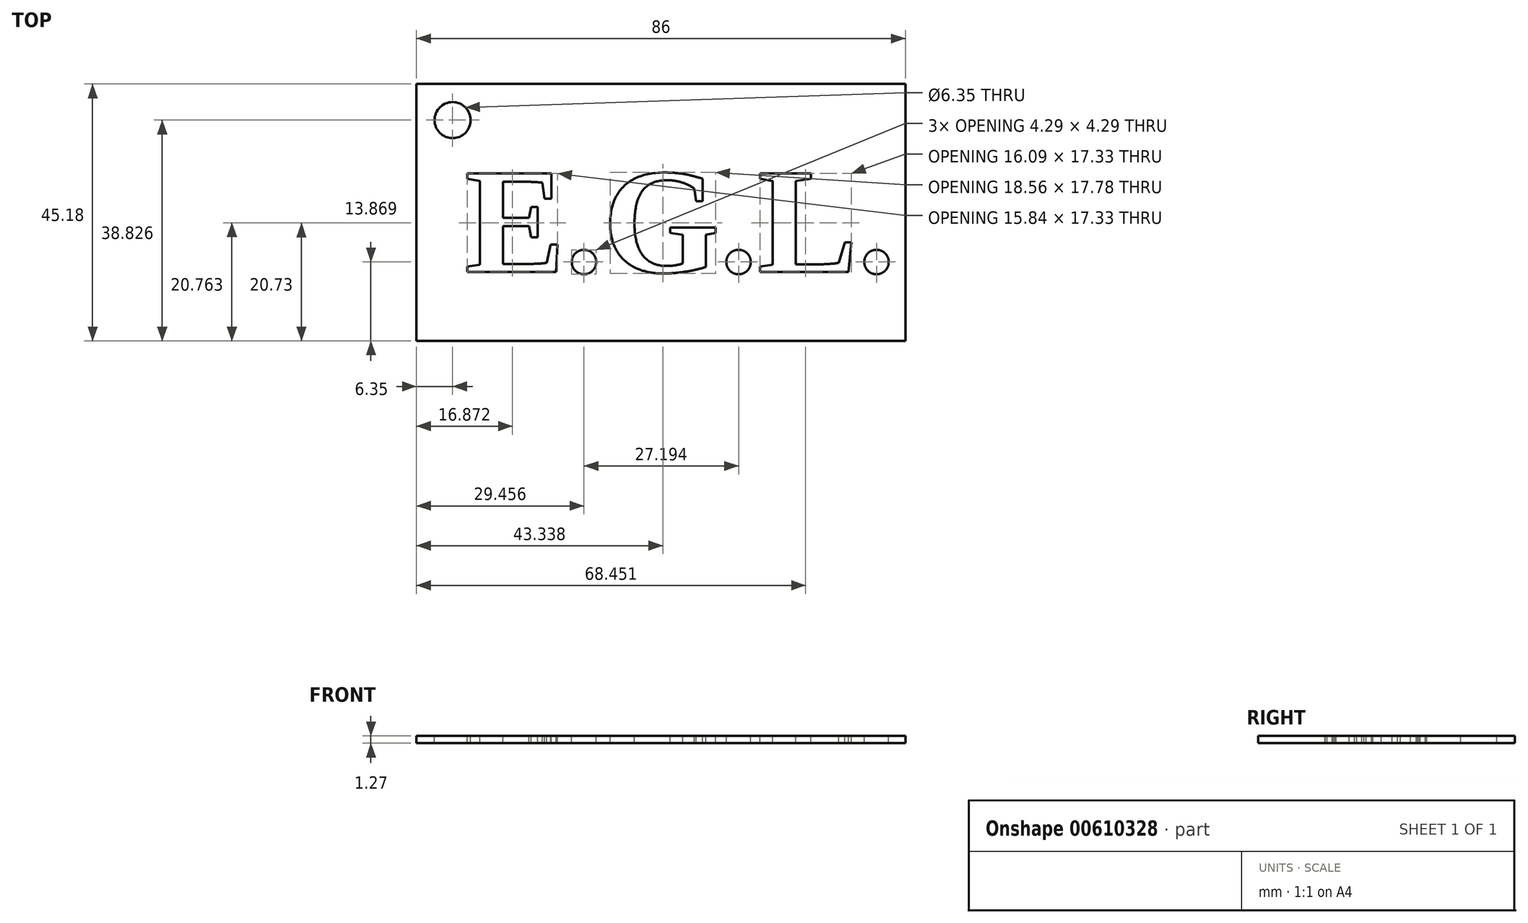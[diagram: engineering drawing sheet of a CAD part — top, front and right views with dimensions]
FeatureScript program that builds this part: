
annotation { "Feature Type Name" : "Feature", "Feature Type Description" : "" }
export const myFeature = defineFeature(function(context is Context, id is Id, definition is map)
    precondition{}
    {
        {
            var Q0;
            Q0=qCreatedBy(makeId("Top.planeOp"),FACE);
            var sketch = newSketch(context, id + "F0", { "sketchPlane" : qUnion([Q0])});
            skLineSegment(sketch, "E0.bottom", {"start": v(-30.55, 23.74) * mm, "end": v(55.45, 23.74) * mm});
            skLineSegment(sketch, "E0.top", {"start": v(-30.55, -21.44) * mm, "end": v(55.45, -21.44) * mm});
            skLineSegment(sketch, "E0.left", {"start": v(-30.55, 23.74) * mm, "end": v(-30.55, -21.44) * mm});
            skLineSegment(sketch, "E0.right", {"start": v(55.45, 23.74) * mm, "end": v(55.45, -21.44) * mm});
            skCircle(sketch, "E1", {"center": v(-24.2, 17.39) * mm, "radius": 3.18 * mm});
            skSolve(sketch);
        }
        {
            var Q0;
            Q0=makeQuery(id+"F0.imprint","IMPRINT",FACE,{"disambiguationData":[TD([[makeQuery(id+"F0.imprint","IMPRINT",EDGE,{"derivedFrom":sQuery(id+"F0.wireOp",EDGE,"E0.bottom")}),-1.0]])]});
            extrude(context, id + "F1", {"entities" : qUnion([Q0]), "oppositeDirection" : true, "depth" : 1.27 * mm, "offsetDistance" : 25.4 * mm});
        }
        {
            var Q0;
            Q0=qCreatedBy(makeId("Top.planeOp"),FACE);
            var sketch = newSketch(context, id + "F2", { "sketchPlane" : qUnion([Q0])});
            skText(sketch, "E2", { "text": "E.G.L.", "fontName": "Tinos-Bold.ttf"});
            const initialGuessF2  = {"E2": [-0.02205, -0.00934, 1, 0, 0.01905]};
            skSetInitialGuess(sketch, initialGuessF2);
            skSolve(sketch);
        }
        {
            var Q0;
            Q0 = qSketchRegion(id + "F2", true);
            extrude(context, id + "F3", {"entities" : qUnion([Q0]), "operationType" : NewBodyOperationType.REMOVE, "oppositeDirection" : true, "depth" : 25.4 * mm, "offsetDistance" : 25.4 * mm});
        }
    });
